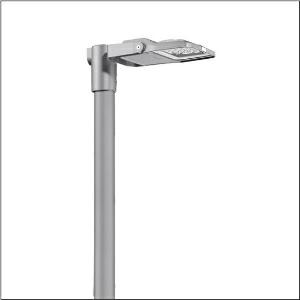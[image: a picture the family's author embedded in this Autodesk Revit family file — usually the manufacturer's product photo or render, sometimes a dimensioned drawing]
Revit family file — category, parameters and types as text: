
# Revit family: floodlight_fl_21_iq_micro___pl61_5xa7761a2c3a_df0f
name_source: partatom
category: Lighting Fixtures
units: mm (PartAtom-declared; Revit-internal decimal feet)

## family parameters
Cut with Voids When Loaded = No
Host = Face
Light Source = No
Part Type = Normal
Room Calculation Point = No
Round Connector Dimension = Use Diameter
Shared = No

## types (1)
- --- (1 x LED, 2910 lm, 23.1 W, 3000K)
    Apparent Load = 23 VA
    CIE Flux Codes = 33 65 98 100 100
    Color Rendering = 70
    Color Temperature = 3000K
    Default Elevation = 1800 mm
    Description = Floodlight FL 21 iQ micro, floodlight, primary light control with lens, of PMMA, primary optical cover: protective disc, of toughened safety glass, transparent, light distribution: PL61, light emission: direct distribution, installation type: surface-mounted, LED, High Power LED, rated luminous flux: 2.910lm, luminous efficacy: 126lm/W, light colour: 730, colour temperature: 3000K, control: optimised constant luminous flux control (CLO 2.0), Desk-Remote (wireless, voltage-free reading and setting of iQ features in the workshop via application-optimized NFC function/RFID function), Light-Fading, Smart-Wire, Night-Set, Lumen-Switch, Temp-Guard, Auto-Match, with terminal, 6-pole, mains connection: 220..240V, AC, 50/60Hz, start of lifetime: 23W, end of service life: 24W, reduction: 11W, luminaire housing, of diecast aluminium, powder-coated, Siteco® metallic grey (DB 702S), corrosivity category C5 mid according to DIN EN ISO 12944, sealing non-destructively replaceable, please order mast flange separately, mast bracket, of steel, galvanised, powder-coated, Siteco® metallic grey (DB 702S), protection rating (complete): IP66, insulation class (complete): insulation class II (safety insulation), certification: CE, ENEC, VDE, protection symbol: D, impact resistance: IK07, permissible operating ambient temperature: -40..+40°C, permissible operating ambient temperature for outdoor applications: -40..+50°C, standard: DIN EN 12944, LABS conformity tested according to VDMA 24364:2018-05, packaging unit: 1 piece

Light Distribution: PL61
    Height = 65 mm
    Lamp = 1 x LED
    Lamp Light Flux = 2910 lm
    Lamp Power = 23.1 W
    Lamp count = 1
    Length = 312 mm
    Luminous efficacy = 126 lm/W
    Manufacturer = Siteco
    ModVariant = No
    Model = 5XA7761A2C3A
    Number of Poles = 1
    OnlyDefault = Yes
    Power Factor = 1
    Product Name = Floodlight FL 21 iQ micro | PL61
    Product group = floodlight | pylon top
    ProductGroupID = 6101
    Protection Class = Protection class II
    Protection Degree = IP 66
    RLX_Detail_Level = 1
    RLX_Emergency_Light_Flux = 0 lm
    RLX_Emergency_Type = 0
    RLX_Emergency_Type_DB = No
    RlxData = <blob elided: 101833 chars, md5=ffa0c5a7>
    Socket = socket
    Standby Power = 0 W
    System Light Flux = 2910 lm
    System Power = 23 W
    Type Comments = factory setting: luminous flux: 100 % | dim-lin: 254 | 455 mA
    Type Image = l_1007121.jpg
    URL = http://relux.com
    VarID = @adj_129127
    Voltage = 0 V
    Weight = 0.00 kg
    Width = 230 mm

## geometry (parser evidence)
native form markers: Blend x4, Sweep x13
no freeform markers — native parametric forms only
